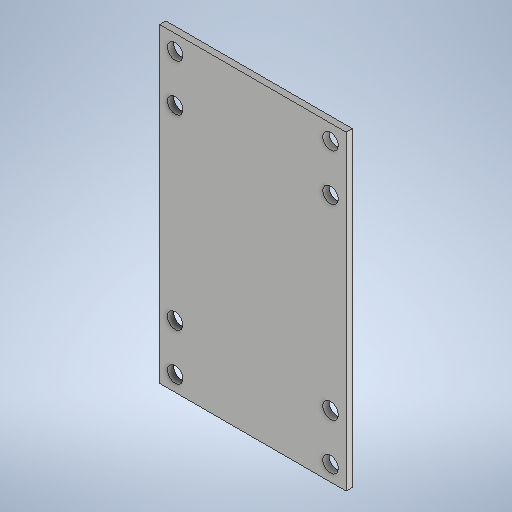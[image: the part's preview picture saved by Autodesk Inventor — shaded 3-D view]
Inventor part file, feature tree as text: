
AUTODESK INVENTOR PART (.ipt)
format: ipt  version: 2025 (Build 290162010, 162A)  size: 284,160 bytes
history: native  units: mm
features: sketch x2, other x2, sheet_metal_op x1, hole x1, mirror x1, projected_geometry x1
ambient origin geometry x8: Origin, YZ Plane, XZ Plane, XY Plane, X Axis, Y Axis, Z Axis, Center Point
bodies: Solid1 (feature_tree)
feature tree (8):
  sheet_metal_op  "Face1"
  hole  "Hole1"  [1 undecoded]
  mirror  "Mirror1"
  sketch  "Sketch1"  dims[d2=8.0mm]
  other  "Plate1"
  sketch  "Sketch2"  dims[d3=20.0mm d4=6.0mm d5=4.0mm d6=2.0mm d7=90.0deg d8=8.0mm d9=20.594885mm d16=240.0mm d17=400.0mm d19=20.0mm d20=20.0mm d21=360.0mm d22=120.0mm d23=120.0mm]
  projected_geometry  "Projected Loop1"
  other  "Definition1"
note: 1 required parameter value undecoded (feature->parameter linkage not recoverable at this tier; creation-order binding heuristic only, values carry confidence <= 0.55)
